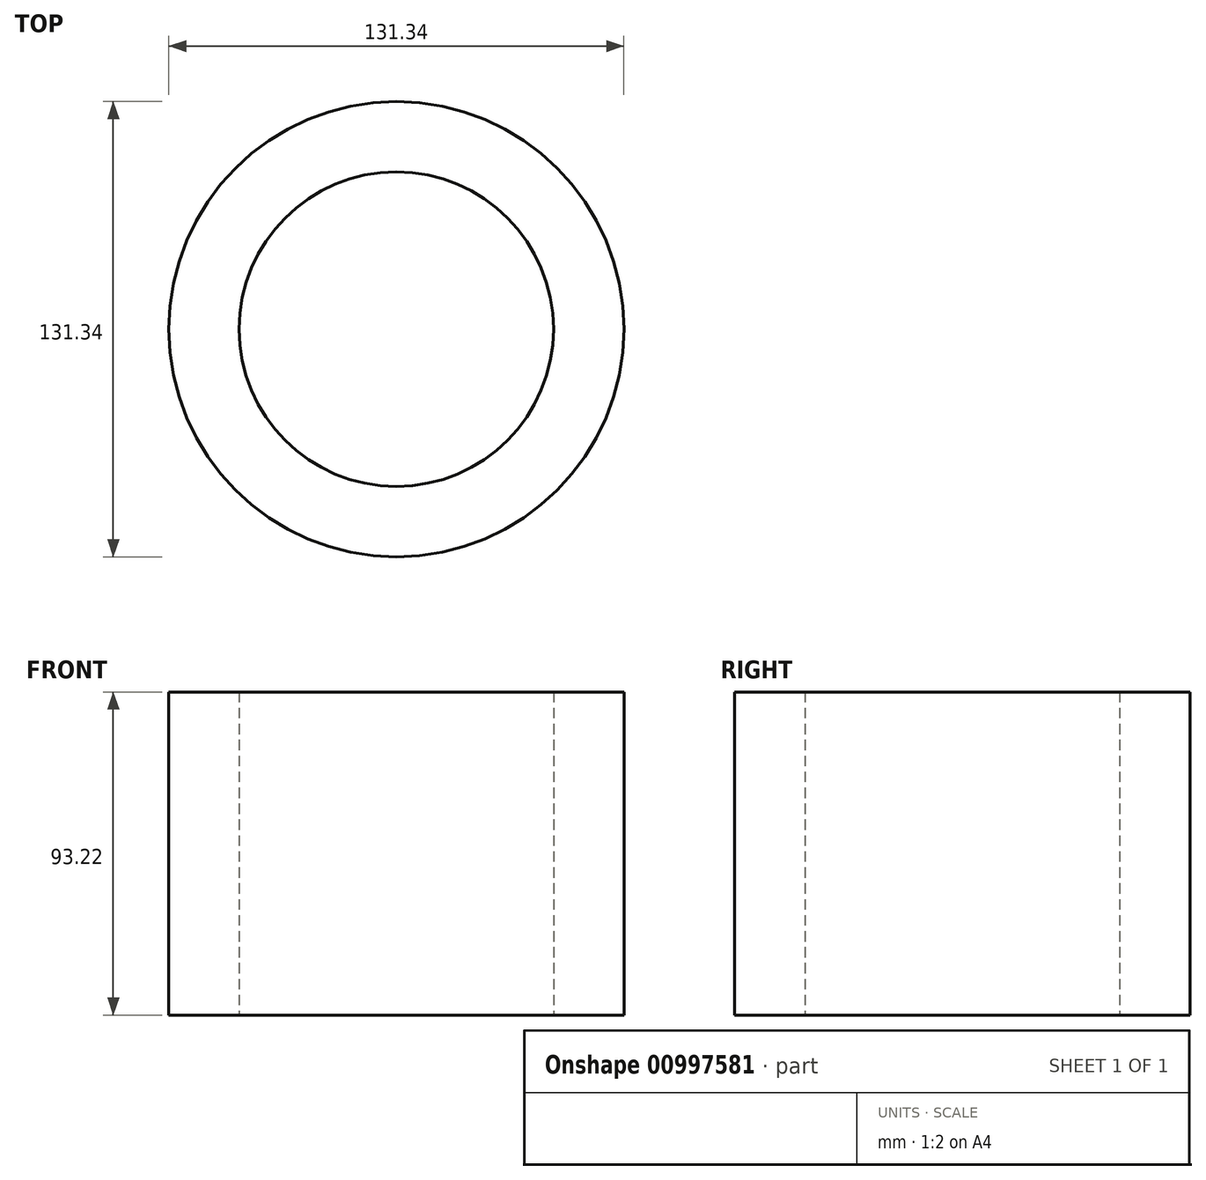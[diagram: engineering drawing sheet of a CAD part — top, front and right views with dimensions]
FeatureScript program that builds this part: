
annotation { "Feature Type Name" : "Feature", "Feature Type Description" : "" }
export const myFeature = defineFeature(function(context is Context, id is Id, definition is map)
    precondition{}
    {
        {
            var Q0;
            Q0=qCreatedBy(makeId("Top.planeOp"),FACE);
            var sketch = newSketch(context, id + "F0", { "sketchPlane" : qUnion([Q0])});
            skCircle(sketch, "E0", {"center": v(0, 0) * mm, "radius": 65.67 * mm});
            skCircle(sketch, "E1", {"center": v(0, 0) * mm, "radius": 45.36 * mm});
            skSolve(sketch);
        }
        {
            var Q0;
            Q0=makeQuery(id+"F0.imprint","IMPRINT",FACE,{"disambiguationData":[TD([[makeQuery(id+"F0.imprint","IMPRINT",EDGE,{"derivedFrom":sQuery(id+"F0.wireOp",EDGE,"E0")}),1.0]])]});
            extrude(context, id + "F1", {"entities" : qUnion([Q0]), "depth" : 93.22 * mm, "offsetDistance" : 25.4 * mm});
        }
    });
